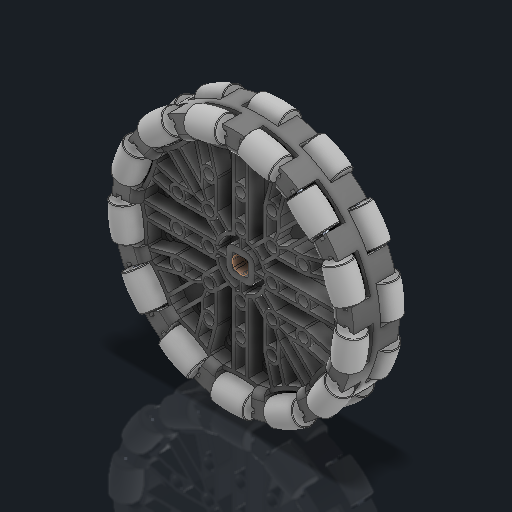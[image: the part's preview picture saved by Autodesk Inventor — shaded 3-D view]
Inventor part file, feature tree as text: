
AUTODESK INVENTOR PART (.ipt)
format: ipt  version: 2023.2 (Build 272271030, 271C)  size: 4,547,072 bytes
history: native  units: in
note: dims shown in document units (in); Inventor stores cm internally (conversion verified against a paired STEP export)
features: other x57, sketch x1
ambient origin geometry x8: Origin, YZ Plane, XZ Plane, XY Plane, X Axis, Y Axis, Z Axis, Center Point
bodies: Solid1 (feature_tree), Solid2 (feature_tree), Solid3 (feature_tree), Solid4 (feature_tree), Solid5 (feature_tree), Solid6 (feature_tree), Solid7 (feature_tree), Solid8 (feature_tree), Solid9 (feature_tree), Solid10 (feature_tree), Solid11 (feature_tree), Solid12 (feature_tree), Solid13 (feature_tree), Solid14 (feature_tree), Solid15 (feature_tree), Solid16 (feature_tree), Solid17 (feature_tree), Solid18 (feature_tree), Solid19 (feature_tree), Solid20 (feature_tree), Solid21 (feature_tree), Solid22 (feature_tree), Solid23 (feature_tree), Solid24 (feature_tree), Solid25 (feature_tree), Solid26 (feature_tree), Solid27 (feature_tree), Solid28 (feature_tree), Solid29 (feature_tree), Solid30 (feature_tree), Solid31 (feature_tree), Solid32 (feature_tree), Solid33 (feature_tree), Solid34 (feature_tree), Solid35 (feature_tree), Solid36 (feature_tree), Solid37 (feature_tree), Solid38 (feature_tree), Solid39 (feature_tree), Solid40 (feature_tree), Solid41 (feature_tree), Solid42 (feature_tree), Solid43 (feature_tree), Solid44 (feature_tree), Solid45 (feature_tree), Solid46 (feature_tree), Solid47 (feature_tree), Solid48 (feature_tree), Solid49 (feature_tree), Solid50 (feature_tree), Solid51 (feature_tree), Solid52 (feature_tree), Solid53 (feature_tree)
feature tree (58):
  other  "4 Omni Antistatic.ipt"
  other  "Solid1::4 Omni Antistatic.ipt"
  other  "Solid2::4 Omni Antistatic.ipt"
  other  "Solid3::4 Omni Antistatic.ipt"
  other  "Solid4::4 Omni Antistatic.ipt"
  other  "Solid5::4 Omni Antistatic.ipt"
  other  "Solid6::4 Omni Antistatic.ipt"
  other  "Solid7::4 Omni Antistatic.ipt"
  other  "Solid8::4 Omni Antistatic.ipt"
  other  "Solid9::4 Omni Antistatic.ipt"
  other  "Solid10::4 Omni Antistatic.ipt"
  other  "Solid11::4 Omni Antistatic.ipt"
  other  "Solid12::4 Omni Antistatic.ipt"
  other  "Solid13::4 Omni Antistatic.ipt"
  other  "Solid14::4 Omni Antistatic.ipt"
  other  "Solid15::4 Omni Antistatic.ipt"
  other  "Solid16::4 Omni Antistatic.ipt"
  other  "Solid17::4 Omni Antistatic.ipt"
  other  "Solid18::4 Omni Antistatic.ipt"
  other  "Solid19::4 Omni Antistatic.ipt"
  other  "Solid20::4 Omni Antistatic.ipt"
  other  "Solid21::4 Omni Antistatic.ipt"
  other  "Solid22::4 Omni Antistatic.ipt"
  other  "Solid23::4 Omni Antistatic.ipt"
  other  "Solid24::4 Omni Antistatic.ipt"
  other  "Solid25::4 Omni Antistatic.ipt"
  other  "Solid26::4 Omni Antistatic.ipt"
  other  "Solid27::4 Omni Antistatic.ipt"
  other  "Solid28::4 Omni Antistatic.ipt"
  other  "Solid29::4 Omni Antistatic.ipt"
  other  "Solid30::4 Omni Antistatic.ipt"
  other  "Solid31::4 Omni Antistatic.ipt"
  other  "Solid32::4 Omni Antistatic.ipt"
  other  "Solid33::4 Omni Antistatic.ipt"
  other  "Solid34::4 Omni Antistatic.ipt"
  other  "Solid35::4 Omni Antistatic.ipt"
  other  "Solid36::4 Omni Antistatic.ipt"
  other  "Solid37::4 Omni Antistatic.ipt"
  other  "Solid38::4 Omni Antistatic.ipt"
  other  "Solid39::4 Omni Antistatic.ipt"
  other  "Solid40::4 Omni Antistatic.ipt"
  other  "Solid41::4 Omni Antistatic.ipt"
  other  "Solid42::4 Omni Antistatic.ipt"
  other  "Solid43::4 Omni Antistatic.ipt"
  other  "Solid44::4 Omni Antistatic.ipt"
  other  "Solid45::4 Omni Antistatic.ipt"
  other  "Solid46::4 Omni Antistatic.ipt"
  other  "Solid47::4 Omni Antistatic.ipt"
  other  "Solid48::4 Omni Antistatic.ipt"
  other  "Solid49::4 Omni Antistatic.ipt"
  other  "Solid50::4 Omni Antistatic.ipt"
  other  "Solid51::4 Omni Antistatic.ipt"
  other  "Solid52::4 Omni Antistatic.ipt"
  other  "Solid53::4 Omni Antistatic.ipt"
  other  "TaggingFeature1"
  sketch  "Sketch1"  dims[d0=0.3937in]
  other  "Srf1"
  other  "Srf1::Derived"
